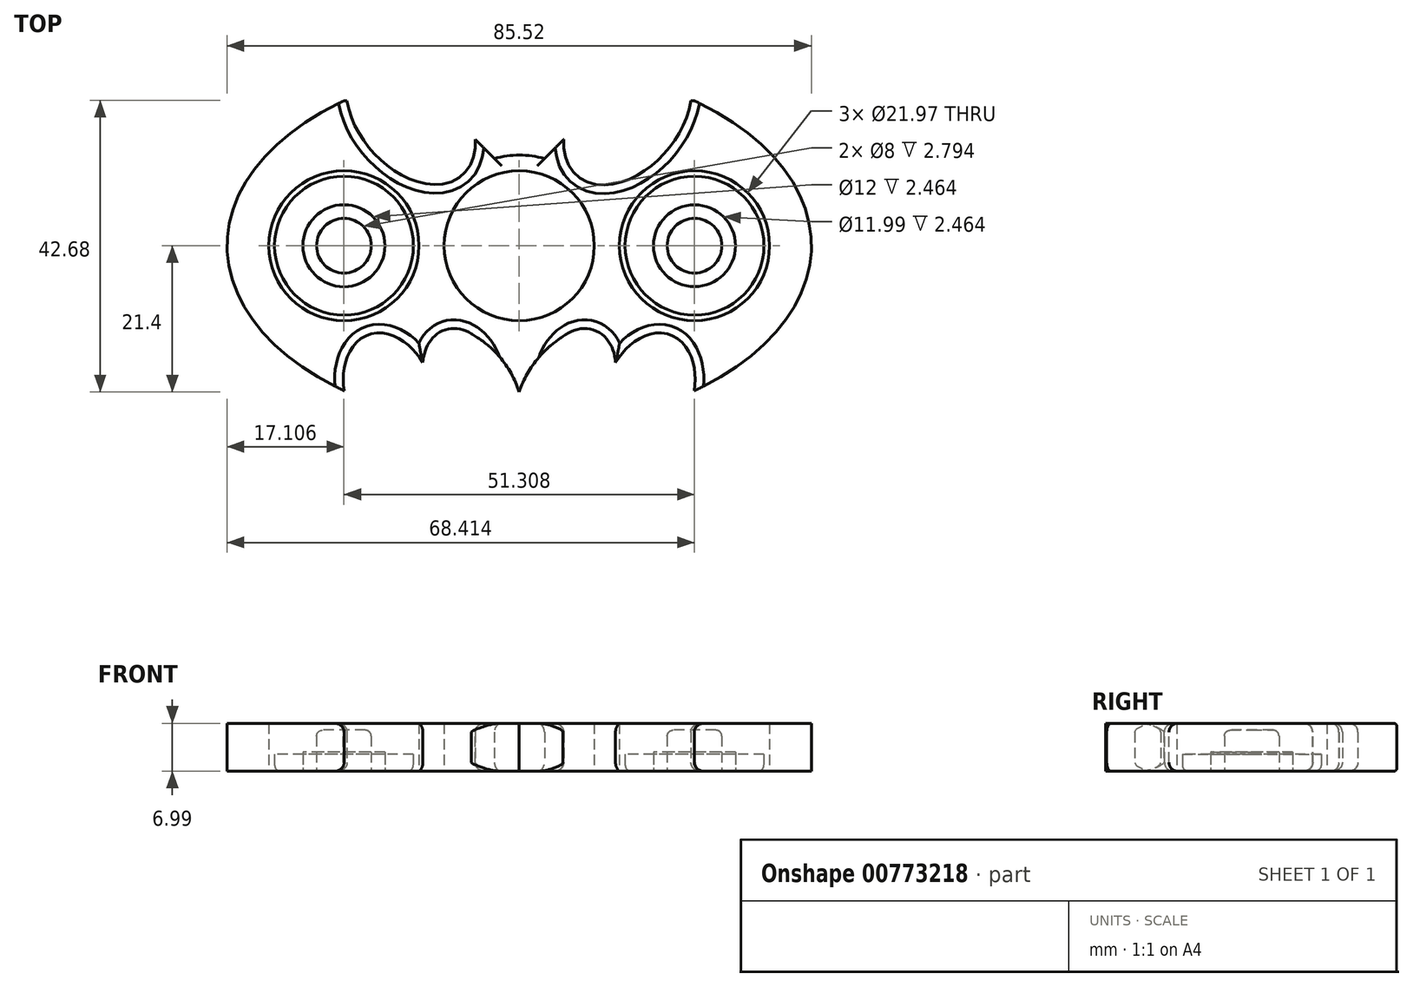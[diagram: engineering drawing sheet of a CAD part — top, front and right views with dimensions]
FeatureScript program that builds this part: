
annotation { "Feature Type Name" : "Feature", "Feature Type Description" : "" }
export const myFeature = defineFeature(function(context is Context, id is Id, definition is map)
    precondition{}
    {
        {
            var Q0;
            Q0=qCreatedBy(makeId("Top.planeOp"),FACE);
            var sketch = newSketch(context, id + "F0", { "sketchPlane" : qUnion([Q0])});
            skCircle(sketch, "E0", {"center": v(0, 0) * mm, "radius": 10.99 * mm});
            skCircle(sketch, "E1", {"center": v(25.65, 0) * mm, "radius": 10.99 * mm});
            skCircle(sketch, "E2", {"center": v(-25.65, 0) * mm, "radius": 10.99 * mm});
            skEllipse(sketch, "E3", {"center": v(0, 0) * mm, "majorRadius": 42.76 * mm, "minorRadius": 26.5 * mm, "majorAxis": v(1, 0)});
            skPoint(sketch, "E4", {"position": v(0, 10.99) * mm});
            skPoint(sketch, "E5", {"position": v(-25.65, 21.2) * mm});
            skLineSegment(sketch, "E6", {"start": v(-25.65, 21.2) * mm, "end": v(25.65, 21.2) * mm});
            skPoint(sketch, "E7", {"position": v(0, 21.2) * mm});
            skPoint(sketch, "E8", {"position": v(-25.6, -10.99) * mm});
            skPoint(sketch, "E9", {"position": v(0.06, -10.99) * mm});
            skPoint(sketch, "E10", {"position": v(25.71, -10.99) * mm});
            skLineSegment(sketch, "E11", {"start": v(-25.6, -10.99) * mm, "end": v(0.06, -10.99) * mm});
            skLineSegment(sketch, "E12", {"start": v(25.71, -10.99) * mm, "end": v(0.06, -10.99) * mm});
            skLineSegment(sketch, "E13", {"start": v(0, 0) * mm, "end": v(-19.73, 23.51) * mm});
            skLineSegment(sketch, "E14", {"start": v(0, 0) * mm, "end": v(19.73, 23.51) * mm});
            skEllipse(sketch, "E15", {"center": v(-15.88, 18.92) * mm, "majorRadius": 11.43 * mm, "minorRadius": 7.62 * mm, "majorAxis": v(0.66, -0.75)});
            skPoint(sketch, "E16", {"position": v(15.87, 18.92) * mm});
            skEllipse(sketch, "E17", {"center": v(15.87, 18.92) * mm, "majorRadius": 11.43 * mm, "minorRadius": 7.62 * mm, "majorAxis": v(-0.64, -0.77)});
            skCircle(sketch, "E18", {"center": v(0, 0) * mm, "radius": 13.26 * mm});
            skLineSegment(sketch, "E19", {"start": v(-6.43, 15.55) * mm, "end": v(6.5, 15.55) * mm});
            skLineSegment(sketch, "E20", {"start": v(-6.43, 15.55) * mm, "end": v(-3.63, 12.76) * mm});
            skLineSegment(sketch, "E21", {"start": v(6.5, 15.55) * mm, "end": v(3.69, 12.74) * mm});
            skLineSegment(sketch, "E22", {"start": v(-25.24, 21.4) * mm, "end": v(0, 21.4) * mm});
            skLineSegment(sketch, "E23", {"start": v(0, 26.5) * mm, "end": v(-1.53, 26.5) * mm});
            skPoint(sketch, "E24", {"position": v(0, -21.4) * mm});
            skLineSegment(sketch, "E25", {"start": v(0, -26.5) * mm, "end": v(1.19, -26.5) * mm});
            skLineSegment(sketch, "E26", {"start": v(0, -21.4) * mm, "end": v(-25.24, -21.4) * mm});
            skLineSegment(sketch, "E27", {"start": v(-25.24, -21.4) * mm, "end": v(0, -21.4) * mm});
            skLineSegment(sketch, "E28", {"start": v(25.24, -21.4) * mm, "end": v(0, -21.4) * mm});
            skEllipse(sketch, "E29", {"center": v(-19.05, -21.4) * mm, "majorRadius": 8.9 * mm, "minorRadius": 6.35 * mm, "majorAxis": v(0.34, -0.94)});
            skEllipse(sketch, "E30", {"center": v(-8.9, -18.35) * mm, "majorRadius": 6.35 * mm, "minorRadius": 5.08 * mm, "majorAxis": v(0.3, -0.95)});
            skArc(sketch, "E31", {"start": v(0, -21.4) * mm, "mid": v(-2.93, -16.21) * mm, "end": v(-7.62, -12.55) * mm});
            skEllipse(sketch, "E32", {"center": v(8.89, -18.35) * mm, "majorRadius": 6.35 * mm, "minorRadius": 5.08 * mm, "majorAxis": v(0.3, 0.95)});
            skEllipse(sketch, "E33", {"center": v(19.05, -21.4) * mm, "majorRadius": 8.9 * mm, "minorRadius": 6.35 * mm, "majorAxis": v(0.34, 0.94)});
            skArc(sketch, "E34", {"start": v(6.41, -13.3) * mm, "mid": v(2.5, -16.78) * mm, "end": v(0, -21.4) * mm});
            skLineSegment(sketch, "E35", {"start": v(19.05, -21.4) * mm, "end": v(22.1, -13.04) * mm});
            skLineSegment(sketch, "E36", {"start": v(-8.9, -18.35) * mm, "end": v(8.9, -18.35) * mm});
            skLineSegment(sketch, "E37", {"start": v(-8.9, -18.35) * mm, "end": v(-10.85, -12.3) * mm});
            skLineSegment(sketch, "E38", {"start": v(8.9, -18.35) * mm, "end": v(10.85, -12.3) * mm});
            skLineSegment(sketch, "E39", {"start": v(-19.05, -21.4) * mm, "end": v(-22.1, -13.04) * mm});
            skCircle(sketch, "E40", {"center": v(-25.65, 0) * mm, "radius": 10.16 * mm});
            skCircle(sketch, "E41", {"center": v(-25.65, 0) * mm, "radius": 4 * mm});
            skCircle(sketch, "E42", {"center": v(-25.65, 0) * mm, "radius": 6 * mm});
            skCircle(sketch, "E43", {"center": v(25.65, 0) * mm, "radius": 10.16 * mm});
            skCircle(sketch, "E44", {"center": v(25.65, 0) * mm, "radius": 6 * mm});
            skCircle(sketch, "E45", {"center": v(25.65, 0) * mm, "radius": 4 * mm});
            skSolve(sketch);
        }
        {
            var Q0;
            Q0=makeQuery(id+"F0.imprint","IMPRINT",FACE,{"disambiguationData":[TD([[makeQuery(id+"F0.imprint","IMPRINT",EDGE,{"derivedFrom":sQuery(id+"F0.wireOp",EDGE,"E2")}),-1.0]])]});
            var Q1;
            {var subQ5=sQuery(id+"F0.wireOp",EDGE,"E20");Q1=makeQuery(id+"F0.imprint","IMPRINT",FACE,{"disambiguationData":[TD([[makeQuery(id+"F0.imprint","IMPRINT",EDGE,{"derivedFrom":subQ5}),-1.0]])]});}
            var Q2;
            {var subQ4=sQuery(id+"F0.wireOp",EDGE,"E0");var subQ6=sQuery(id+"F0.wireOp",EDGE,"E13");var subQ7=makeQuery(id+"F0.imprint","INTERSECT",VERTEX,{"derivedFrom":[subQ4,subQ6]});Q2=makeQuery(id+"F0.imprint","IMPRINT",FACE,{"disambiguationData":[TD([[makeQuery(id+"F0.imprint","IMPRINT",EDGE,{"disambiguationData":[TD([[subQ7,1.0]])],"derivedFrom":subQ4}),-1.0]])]});}
            var Q3;
            {var subQ0=sQuery(id+"F0.wireOp",EDGE,"E11");var subQ1=sQuery(id+"F0.wireOp",EDGE,"E0");var subQ2=makeQuery(id+"F0.imprint","INTERSECT",VERTEX,{"derivedFrom":[subQ1,subQ0]});Q3=makeQuery(id+"F0.imprint","IMPRINT",FACE,{"disambiguationData":[TD([[makeQuery(id+"F0.imprint","IMPRINT",EDGE,{"disambiguationData":[TD([[subQ2,1.0]])],"derivedFrom":subQ1}),-1.0]])]});}
            var Q4;
            {var subQ5=sQuery(id+"F0.wireOp",EDGE,"E21");Q4=makeQuery(id+"F0.imprint","IMPRINT",FACE,{"disambiguationData":[TD([[makeQuery(id+"F0.imprint","IMPRINT",EDGE,{"derivedFrom":subQ5}),1.0]])]});}
            var Q5;
            {var subQ0=sQuery(id+"F0.wireOp",EDGE,"E12");var subQ1=sQuery(id+"F0.wireOp",EDGE,"E0");var subQ2=makeQuery(id+"F0.imprint","INTERSECT",VERTEX,{"derivedFrom":[subQ1,subQ0]});Q5=makeQuery(id+"F0.imprint","IMPRINT",FACE,{"disambiguationData":[TD([[makeQuery(id+"F0.imprint","IMPRINT",EDGE,{"disambiguationData":[TD([[subQ2,-1.0]])],"derivedFrom":subQ1}),-1.0]])]});}
            var Q6;
            {var subQ0=sQuery(id+"F0.wireOp",EDGE,"E11");var subQ1=sQuery(id+"F0.wireOp",EDGE,"E0");var subQ2=makeQuery(id+"F0.imprint","INTERSECT",VERTEX,{"derivedFrom":[subQ1,subQ0]});Q6=makeQuery(id+"F0.imprint","IMPRINT",FACE,{"disambiguationData":[TD([[makeQuery(id+"F0.imprint","IMPRINT",EDGE,{"disambiguationData":[TD([[subQ2,-1.0]])],"derivedFrom":subQ1}),-1.0]])]});}
            var Q7;
            {var subQ1=sQuery(id+"F0.wireOp",EDGE,"E31");var subQ3=sQuery(id+"F0.wireOp",EDGE,"E36");var subQ4=makeQuery(id+"F0.imprint","INTERSECT",VERTEX,{"derivedFrom":[subQ1,subQ3]});Q7=makeQuery(id+"F0.imprint","IMPRINT",FACE,{"disambiguationData":[TD([[makeQuery(id+"F0.imprint","IMPRINT",EDGE,{"disambiguationData":[TD([[subQ4,-1.0]])],"derivedFrom":subQ3}),-1.0]])]});}
            extrude(context, id + "F1", {"entities" : qUnion([Q0, Q1, Q2, Q3, Q4, Q5, Q6, Q7]), "depth" : 7 * mm, "offsetDistance" : 25.4 * mm});
        }
        {
            var Q0;
            Q0=makeQuery(id+"F1.opExtrude","CAP_EDGE",EDGE,{"disambiguationData":[OSD([sQuery(id+"F0.wireOp",EDGE,"E15")])],"isStart":false});
            var Q1;
            Q1=makeQuery(id+"F1.opExtrude","CAP_EDGE",EDGE,{"disambiguationData":[OSD([sQuery(id+"F0.wireOp",EDGE,"E17")])],"isStart":false});
            var Q2;
            Q2=makeQuery(id+"F1.opExtrude","CAP_EDGE",EDGE,{"disambiguationData":[OSD([sQuery(id+"F0.wireOp",EDGE,"E18")])],"isStart":false});
            var Q3;
            Q3=makeQuery(id+"F1.opExtrude","CAP_EDGE",EDGE,{"disambiguationData":[OSD([sQuery(id+"F0.wireOp",EDGE,"E32")])],"isStart":false});
            var Q4;
            Q4=makeQuery(id+"F1.opExtrude","CAP_EDGE",EDGE,{"disambiguationData":[OSD([sQuery(id+"F0.wireOp",EDGE,"E33")])],"isStart":false});
            var Q5;
            Q5=makeQuery(id+"F1.opExtrude","CAP_EDGE",EDGE,{"disambiguationData":[OSD([sQuery(id+"F0.wireOp",EDGE,"E30")])],"isStart":false});
            var Q6;
            Q6=makeQuery(id+"F1.opExtrude","CAP_EDGE",EDGE,{"disambiguationData":[OSD([sQuery(id+"F0.wireOp",EDGE,"E29")])],"isStart":false});
            var Q7;
            Q7=makeQuery(id+"F1.opExtrude","CAP_EDGE",EDGE,{"disambiguationData":[OSD([sQuery(id+"F0.wireOp",EDGE,"E18")])],"isStart":true});
            var Q8;
            Q8=makeQuery(id+"F1.opExtrude","CAP_EDGE",EDGE,{"disambiguationData":[OSD([sQuery(id+"F0.wireOp",EDGE,"E17")])],"isStart":true});
            var Q9;
            Q9=makeQuery(id+"F1.opExtrude","CAP_EDGE",EDGE,{"disambiguationData":[OSD([sQuery(id+"F0.wireOp",EDGE,"E15")])],"isStart":true});
            var Q10;
            Q10=makeQuery(id+"F1.opExtrude","CAP_EDGE",EDGE,{"disambiguationData":[OSD([sQuery(id+"F0.wireOp",EDGE,"E33")])],"isStart":true});
            var Q11;
            Q11=makeQuery(id+"F1.opExtrude","CAP_EDGE",EDGE,{"disambiguationData":[OSD([sQuery(id+"F0.wireOp",EDGE,"E32")])],"isStart":true});
            var Q12;
            Q12=makeQuery(id+"F1.opExtrude","CAP_EDGE",EDGE,{"disambiguationData":[OSD([sQuery(id+"F0.wireOp",EDGE,"E30")])],"isStart":true});
            var Q13;
            Q13=makeQuery(id+"F1.opExtrude","CAP_EDGE",EDGE,{"disambiguationData":[OSD([sQuery(id+"F0.wireOp",EDGE,"E29")])],"isStart":true});
            fillet(context, id + "F2", {"entities" : qUnion([Q0, Q1, Q2, Q3, Q4, Q5, Q6, Q7, Q8, Q9, Q10, Q11, Q12, Q13]), "radius" : 1.27 * mm, "tangentPropagation" : true, "allowEdgeOverflow" : false});
        }
        {
            var Q0;
            Q0=makeQuery(id+"F0.imprint","IMPRINT",FACE,{"disambiguationData":[TD([[makeQuery(id+"F0.imprint","IMPRINT",EDGE,{"derivedFrom":sQuery(id+"F0.wireOp",EDGE,"E40")}),1.0]])]});
            var Q1;
            Q1=makeQuery(id+"F0.imprint","IMPRINT",FACE,{"disambiguationData":[TD([[makeQuery(id+"F0.imprint","IMPRINT",EDGE,{"derivedFrom":sQuery(id+"F0.wireOp",EDGE,"E43")}),1.0]])]});
            extrude(context, id + "F3", {"entities" : qUnion([Q0, Q1]), "operationType" : NewBodyOperationType.ADD, "depth" : 2.46 * mm, "offsetDistance" : 25.4 * mm});
        }
        {
            var Q0;
            Q0=makeQuery(id+"F0.imprint","IMPRINT",FACE,{"disambiguationData":[TD([[makeQuery(id+"F0.imprint","IMPRINT",EDGE,{"derivedFrom":sQuery(id+"F0.wireOp",EDGE,"E41")}),-1.0]])]});
            var Q1;
            Q1=makeQuery(id+"F0.imprint","IMPRINT",FACE,{"disambiguationData":[TD([[makeQuery(id+"F0.imprint","IMPRINT",EDGE,{"derivedFrom":sQuery(id+"F0.wireOp",EDGE,"E44")}),1.0]])]});
            extrude(context, id + "F4", {"entities" : qUnion([Q0, Q1]), "depth" : 2.8 * mm, "offsetDistance" : 25.4 * mm});
        }
        {
            var Q0;
            Q0=makeQuery(id+"F0.imprint","IMPRINT",FACE,{"disambiguationData":[TD([[makeQuery(id+"F0.imprint","IMPRINT",EDGE,{"derivedFrom":sQuery(id+"F0.wireOp",EDGE,"E41")}),1.0]])]});
            var Q1;
            Q1=makeQuery(id+"F0.imprint","IMPRINT",FACE,{"disambiguationData":[TD([[makeQuery(id+"F0.imprint","IMPRINT",EDGE,{"derivedFrom":sQuery(id+"F0.wireOp",EDGE,"E45")}),1.0]])]});
            extrude(context, id + "F5", {"entities" : qUnion([Q0, Q1]), "depth" : 6 * mm, "offsetDistance" : 25.4 * mm});
        }
        {
            var Q0;
            Q0=makeQuery(id+"F3.opExtrude","CAP_EDGE",EDGE,{"disambiguationData":[OSD([sQuery(id+"F0.wireOp",EDGE,"E43")])],"isStart":true});
            var Q1;
            Q1=makeQuery(id+"F3.opExtrude","CAP_EDGE",EDGE,{"disambiguationData":[OSD([sQuery(id+"F0.wireOp",EDGE,"E40")])],"isStart":true});
            var Q2;
            Q2=makeQuery(id+"F5.opExtrude","CAP_EDGE",EDGE,{"disambiguationData":[OSD([sQuery(id+"F0.wireOp",EDGE,"E41")])],"isStart":false});
            var Q3;
            Q3=makeQuery(id+"F5.opExtrude","CAP_EDGE",EDGE,{"disambiguationData":[OSD([sQuery(id+"F0.wireOp",EDGE,"E45")])],"isStart":false});
            fillet(context, id + "F6", {"entities" : qUnion([Q0, Q1, Q2, Q3]), "radius" : 0.89 * mm, "tangentPropagation" : true, "allowEdgeOverflow" : false});
        }
    });
